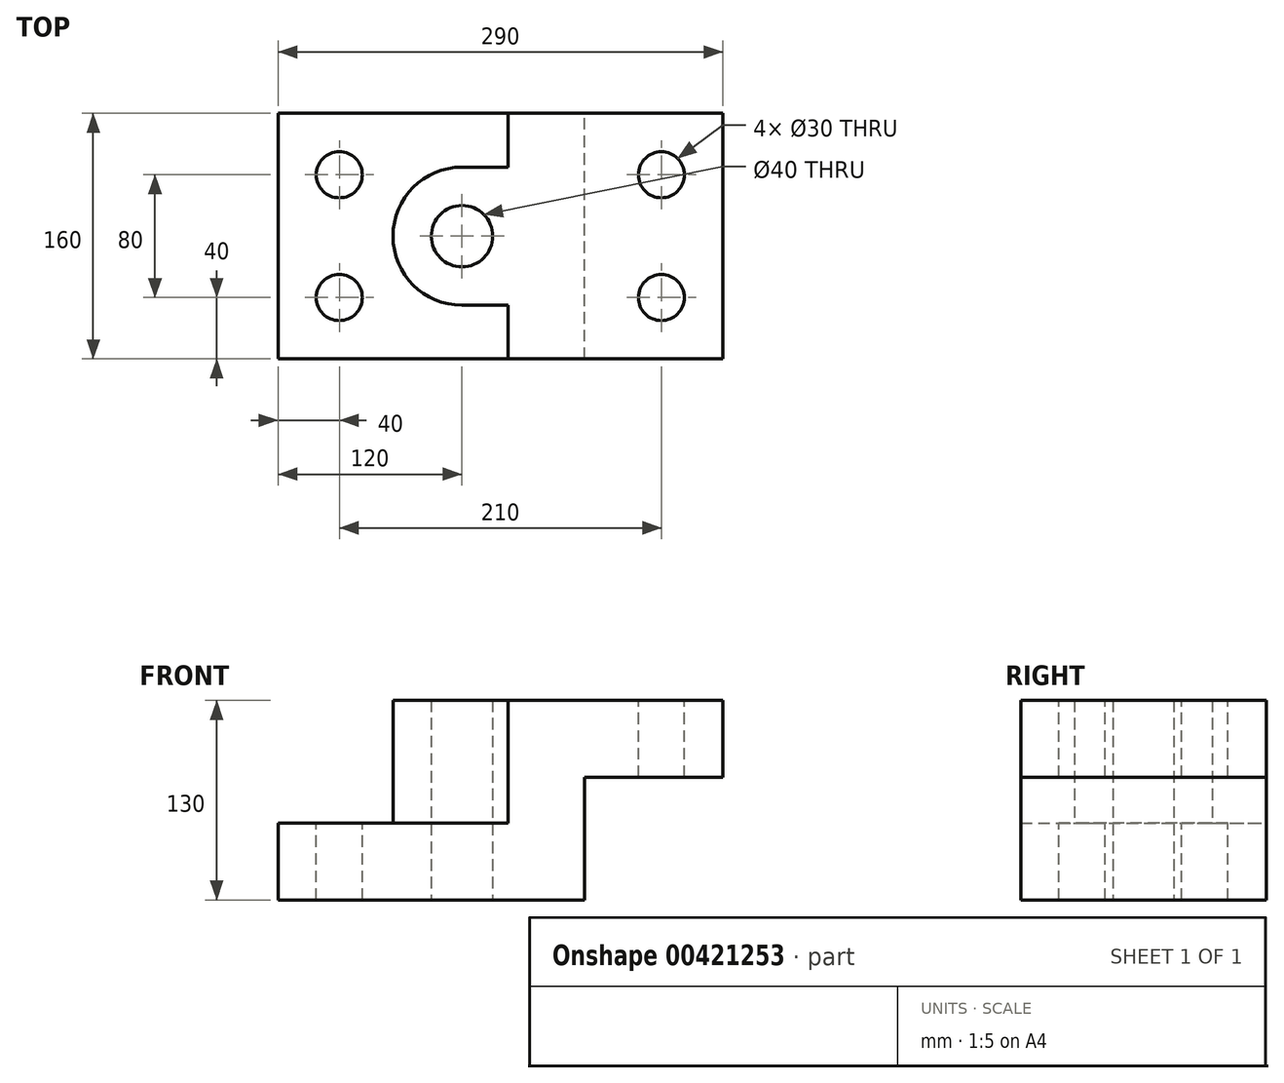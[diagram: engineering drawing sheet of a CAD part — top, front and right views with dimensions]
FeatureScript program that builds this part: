
annotation { "Feature Type Name" : "Feature", "Feature Type Description" : "" }
export const myFeature = defineFeature(function(context is Context, id is Id, definition is map)
    precondition{}
    {
        {
            var Q0;
            Q0=qCreatedBy(makeId("Front.planeOp"),FACE);
            var sketch = newSketch(context, id + "F0", { "sketchPlane" : qUnion([Q0])});
            skLineSegment(sketch, "E0.bottom", {"start": v(-150, 0) * mm, "end": v(0, 0) * mm});
            skLineSegment(sketch, "E0.top", {"start": v(-150, -50) * mm, "end": v(50, -50) * mm});
            skLineSegment(sketch, "E0.left", {"start": v(-150, 0) * mm, "end": v(-150, -50) * mm});
            skLineSegment(sketch, "E1.left", {"start": v(0, 0) * mm, "end": v(0, 80) * mm});
            skLineSegment(sketch, "E1.right", {"start": v(50, -50) * mm, "end": v(50, 30) * mm});
            skLineSegment(sketch, "E2.bottom", {"start": v(0, 80) * mm, "end": v(140, 80) * mm});
            skLineSegment(sketch, "E2.top", {"start": v(50, 30) * mm, "end": v(140, 30) * mm});
            skLineSegment(sketch, "E2.right", {"start": v(140, 80) * mm, "end": v(140, 30) * mm});
            skSolve(sketch);
        }
        {
            var Q0;
            Q0=makeQuery(id+"F0.imprint","IMPRINT",FACE,{"disambiguationData":[TD([[makeQuery(id+"F0.imprint","IMPRINT",EDGE,{"derivedFrom":sQuery(id+"F0.wireOp",EDGE,"E0.bottom")}),-1.0]])]});
            extrude(context, id + "F1", {"entities" : qUnion([Q0]), "endBound" : BoundingType.SYMMETRIC, "depth" : 160 * mm});
        }
        {
            var Q0;
            Q0=makeQuery(id+"F1.opExtrude","SWEPT_FACE",FACE,{"disambiguationData":[OSD([sQuery(id+"F0.wireOp",EDGE,"E0.bottom")])]});
            var sketch = newSketch(context, id + "F2", { "sketchPlane" : qUnion([Q0])});
            skLineSegment(sketch, "E3", {"start": v(0, 45) * mm, "end": v(-30, 45) * mm});
            skLineSegment(sketch, "E4", {"start": v(0, -45) * mm, "end": v(-30, -45) * mm});
            skArc(sketch, "E5", {"start": v(-30, 45) * mm, "mid": v(-75, 0) * mm, "end": v(-30, -45) * mm});
            skCircle(sketch, "E6", {"center": v(-30, 0) * mm, "radius": 20 * mm});
            skLineSegment(sketch, "E7", {"start": v(0, 45) * mm, "end": v(0, -45) * mm});
            skCircle(sketch, "E8", {"center": v(-110, 40) * mm, "radius": 15 * mm});
            skCircle(sketch, "E9", {"center": v(-110, -40) * mm, "radius": 15 * mm});
            skCircle(sketch, "E10", {"center": v(100, 40) * mm, "radius": 15 * mm});
            skCircle(sketch, "E11", {"center": v(100, -40) * mm, "radius": 15 * mm});
            skSolve(sketch);
        }
        {
            var Q0;
            Q0=makeQuery(id+"F2.imprint","IMPRINT",FACE,{"disambiguationData":[TD([[makeQuery(id+"F2.imprint","IMPRINT",EDGE,{"derivedFrom":sQuery(id+"F2.wireOp",EDGE,"E3")}),1.0]])]});
            extrude(context, id + "F3", {"entities" : qUnion([Q0]), "operationType" : NewBodyOperationType.ADD, "depth" : 80 * mm});
        }
        {
            var Q0;
            Q0=makeQuery(id+"F2.imprint","IMPRINT",FACE,{"disambiguationData":[TD([[makeQuery(id+"F2.imprint","IMPRINT",EDGE,{"derivedFrom":sQuery(id+"F2.wireOp",EDGE,"E8")}),1.0]])]});
            var Q1;
            Q1=makeQuery(id+"F2.imprint","IMPRINT",FACE,{"disambiguationData":[TD([[makeQuery(id+"F2.imprint","IMPRINT",EDGE,{"derivedFrom":sQuery(id+"F2.wireOp",EDGE,"E9")}),1.0]])]});
            var Q2;
            Q2=makeQuery(id+"F2.imprint","IMPRINT",FACE,{"disambiguationData":[TD([[makeQuery(id+"F2.imprint","IMPRINT",EDGE,{"derivedFrom":sQuery(id+"F2.wireOp",EDGE,"E11")}),1.0]])]});
            var Q3;
            Q3=makeQuery(id+"F2.imprint","IMPRINT",FACE,{"disambiguationData":[TD([[makeQuery(id+"F2.imprint","IMPRINT",EDGE,{"derivedFrom":sQuery(id+"F2.wireOp",EDGE,"E10")}),1.0]])]});
            var Q4;
            Q4=makeQuery(id+"F2.imprint","IMPRINT",FACE,{"disambiguationData":[TD([[makeQuery(id+"F2.imprint","IMPRINT",EDGE,{"derivedFrom":sQuery(id+"F2.wireOp",EDGE,"E6")}),1.0]])]});
            extrude(context, id + "F4", {"entities" : qUnion([Q0, Q1, Q2, Q3, Q4]), "operationType" : NewBodyOperationType.REMOVE, "endBound" : BoundingType.THROUGH_ALL, "oppositeDirection" : true, "depth" : 25 * mm, "hasSecondDirection" : true, "secondDirectionBound" : SecondDirectionBoundingType.THROUGH_ALL, "secondDirectionOppositeDirection" : false, "secondDirectionDepth" : 25 * mm});
        }
    });
